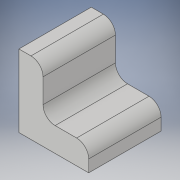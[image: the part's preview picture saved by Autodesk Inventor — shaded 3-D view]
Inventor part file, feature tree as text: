
AUTODESK INVENTOR PART (.ipt)
format: ipt  version: 2018 (Build 220112000, 112)  size: 106,496 bytes
history: native  units: in
note: dims shown in document units (in); Inventor stores cm internally (conversion verified against a paired STEP export)
features: extrude x1, fillet x1, sketch x1
ambient origin geometry x8: Origin, YZ Plane, XZ Plane, XY Plane, X Axis, Y Axis, Z Axis, Center Point
bodies: Solid1 (feature_tree)
feature tree (3):
  extrude  "Extrusion1"  Depth=0.5in
  fillet  "Fillet3"  Radius=1.0in
  sketch  "Sketch1"  dims[d0=1.5in d1=0.5in d2=1.0in d3=1.5in d4=0.0in d13=0.25in]
